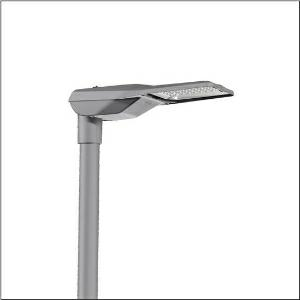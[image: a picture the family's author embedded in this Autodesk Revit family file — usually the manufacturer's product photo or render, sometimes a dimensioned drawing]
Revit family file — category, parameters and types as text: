
# Revit family: streetlight_sl_21_mini___st0_5a_5xe2b33s08gb_907c
name_source: partatom
category: Lighting Fixtures
units: mm (PartAtom-declared; Revit-internal decimal feet)

## family parameters
Cut with Voids When Loaded = No
Host = Face
Light Source = No
Part Type = Normal
Room Calculation Point = No
Round Connector Dimension = Use Diameter
Shared = No

## types (1)
- --- (1 x LED, 5940 lm, 40.4 W, 3000K)
    Apparent Load = 40 VA
    CIE Flux Codes = 41 75 97 100 100
    Color Rendering = 70
    Color Temperature = 3000K
    Default Elevation = 1800 mm
    Description = Streetlight SL 21 mini, mast luminaire, primary light control with lens, of PMMA, primary optical cover: cover, of toughened safety glass, transparent, light distribution: ST0.5a, light emission: direct distribution, primary light characteristic: asymmetric, installation type: side-entry, post-top, LED, High Power LED, rated luminous flux: 5.940lm, luminous efficacy: 147lm/W, light colour: 730, colour temperature: 3000K, control gear: D4i, control: overheat protection, constant luminous flux control, time-dependent luminous flux control, flexible luminous flux parameterisation, pre-setting: logarithmic dimming characteristic, mains connection: 220..240V, AC, 50/60Hz, start of lifetime: 40W, end of service life: 41W, reduction: 19W, luminaire housing, of diecast aluminium, powder-coated, SITECO metallic grey (DB 702S), corrosivity category C5 high according to DIN EN ISO 12944, please order mast flange separately, inclination adjustable: 0°, 5°, 10°, 15°, sealing non-destructively replaceable, multi-level sealing system, length: 628mm, width: 235mm, height: 110mm, mast flange for spigot size: 42mm (side-entry): 5XC10008XM4, 60/48mm (side-entry/post-top): 5XC10108XM2, 76/60mm (side-entry/post-top): 5XC10108XM1, mounting height: 4..8m, Smart Interface above, protection rating (complete): IP66, insulation class (complete): insulation class II (safety insulation), certification: CE, ENEC, ENEC+, VDE, impact resistance: IK10, permissible operating ambient temperature for outdoor applications: -40..+50°C, standard-compliant lighting for roads and squares, packaging unit: 1 piece

Light Distribution: ST0.5a
    Height = 110 mm
    Lamp = 1 x LED
    Lamp Light Flux = 5940 lm
    Lamp Power = 40.4 W
    Lamp count = 1
    Length = 625 mm
    Luminous efficacy = 147 lm/W
    Manufacturer = Siteco
    ModVariant = No
    Model = 5XE2B33S08GB
    Number of Poles = 1
    OnlyDefault = Yes
    Power Factor = 1
    Product Name = Streetlight SL 21 mini | ST0.5a
    Product group = mast luminaire | pylon top
    ProductGroupID = 6100
    Protection Class = Protection class II
    Protection Degree = IP 66
    RLX_Detail_Level = 1
    RLX_Emergency_Light_Flux = 0 lm
    RLX_Emergency_Type = 0
    RLX_Emergency_Type_DB = No
    RlxData = <blob elided: 37169 chars, md5=d52952ee>
    Socket = socket
    Standby Power = 0 W
    System Light Flux = 5940 lm
    System Power = 40 W
    Type Comments = factory setting: luminous flux: 100 % | dim-lin: 254 | 812 mA
    Type Image = l_1003515.jpg
    URL = http://relux.com
    VarID = @adj_188725
    Voltage = 0 V
    Weight = 0.00 kg
    Width = 234 mm

## geometry (parser evidence)
native form markers: Blend x4, Sweep x8
no freeform markers — native parametric forms only
